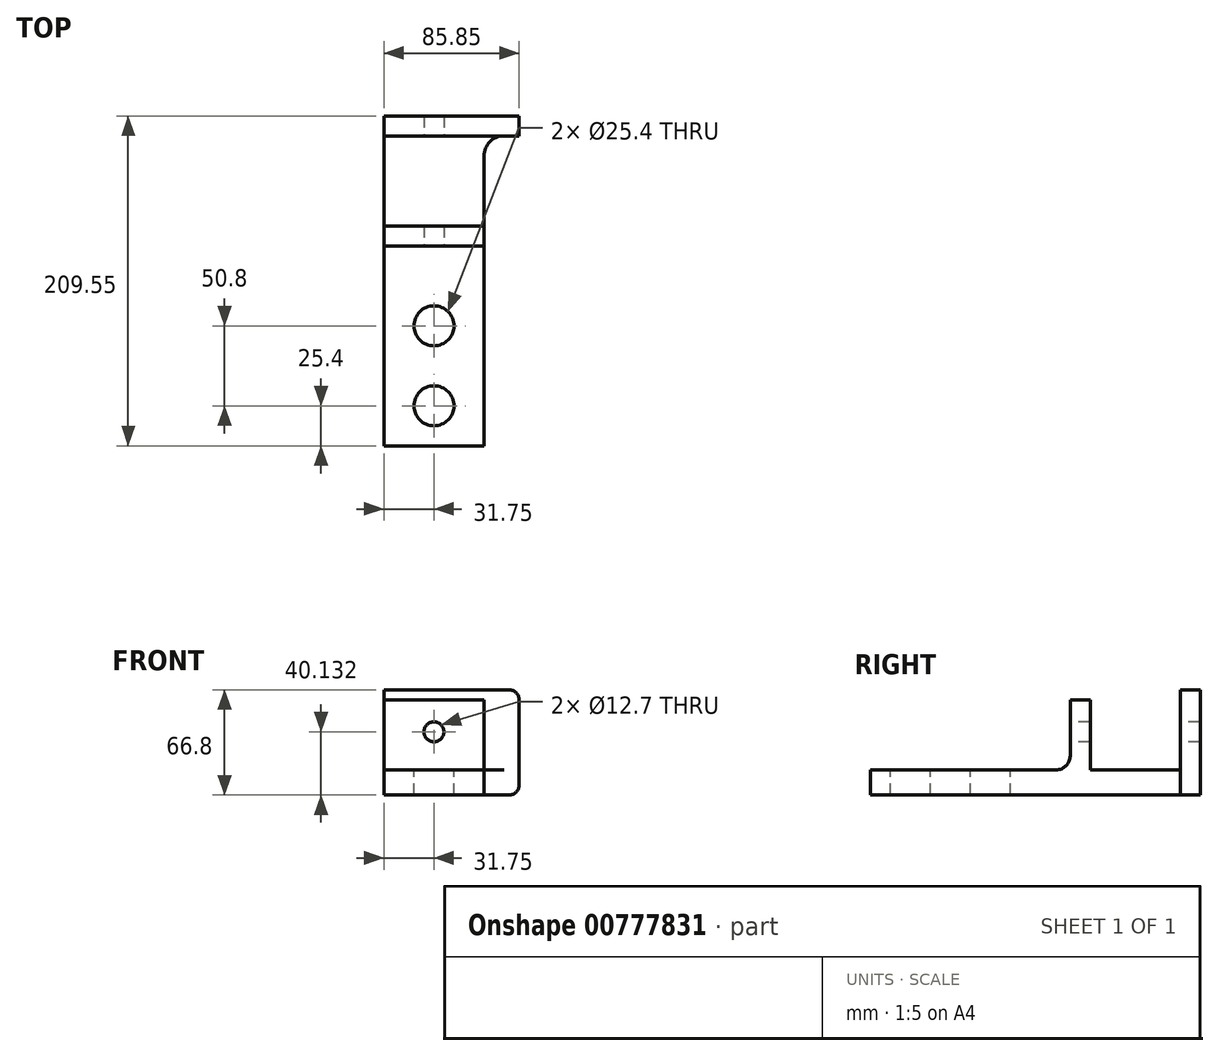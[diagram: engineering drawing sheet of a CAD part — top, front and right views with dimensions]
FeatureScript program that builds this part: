
annotation { "Feature Type Name" : "Feature", "Feature Type Description" : "" }
export const myFeature = defineFeature(function(context is Context, id is Id, definition is map)
    precondition{}
    {
        {
            var Q0;
            Q0=qCreatedBy(makeId("Right.planeOp"),FACE);
            var sketch = newSketch(context, id + "F0", { "sketchPlane" : qUnion([Q0])});
            skLineSegment(sketch, "E0", {"start": v(0, 0) * mm, "end": v(0, 66.8) * mm});
            skLineSegment(sketch, "E1", {"start": v(0, 66.8) * mm, "end": v(-12.7, 66.8) * mm});
            skLineSegment(sketch, "E2", {"start": v(-12.7, 66.8) * mm, "end": v(-12.7, 16) * mm});
            skLineSegment(sketch, "E3", {"start": v(-12.7, 16) * mm, "end": v(-69.85, 16) * mm});
            skLineSegment(sketch, "E4", {"start": v(-69.85, 16) * mm, "end": v(-69.85, 60.45) * mm});
            skLineSegment(sketch, "E5", {"start": v(-69.85, 60.45) * mm, "end": v(-82.55, 60.45) * mm});
            skLineSegment(sketch, "E6", {"start": v(-82.55, 60.45) * mm, "end": v(-82.55, 24.9) * mm});
            skLineSegment(sketch, "E7", {"start": v(-91.44, 16) * mm, "end": v(-209.55, 16) * mm});
            skLineSegment(sketch, "E8", {"start": v(-209.55, 16) * mm, "end": v(-209.55, 0) * mm});
            skLineSegment(sketch, "E9", {"start": v(-209.55, 0) * mm, "end": v(0, 0) * mm});
            skPoint(sketch, "E10.visualSharp", {"position": v(-82.55, 16) * mm});
            skArc(sketch, "E10.filletArc", {"start": v(-91.44, 16) * mm, "mid": v(-85.15, 18.6) * mm, "end": v(-82.55, 24.9) * mm});
            skSolve(sketch);
        }
        {
            var Q0;
            Q0 = qSketchRegion(id + "F0", true);
            extrude(context, id + "F1", {"entities" : qUnion([Q0]), "depth" : 54.1 * mm, "offsetDistance" : 25.4 * mm, "hasSecondDirection" : true, "secondDirectionOppositeDirection" : true, "secondDirectionDepth" : 31.75 * mm});
        }
        {
            var Q0;
            Q0=qCreatedBy(makeId("Top.planeOp"),FACE);
            var sketch = newSketch(context, id + "F2", { "sketchPlane" : qUnion([Q0])});
            skLineSegment(sketch, "E11.bottom", {"start": v(54.1, -209.55) * mm, "end": v(31.75, -209.55) * mm});
            skLineSegment(sketch, "E11.top", {"start": v(54.1, -12.7) * mm, "end": v(44.45, -12.7) * mm});
            skLineSegment(sketch, "E11.left", {"start": v(54.1, -209.55) * mm, "end": v(54.1, -12.7) * mm});
            skLineSegment(sketch, "E11.right", {"start": v(31.75, -209.55) * mm, "end": v(31.75, -25.4) * mm});
            skPoint(sketch, "E12.visualSharp", {"position": v(31.75, -12.7) * mm});
            skArc(sketch, "E12.filletArc", {"start": v(44.45, -12.7) * mm, "mid": v(35.47, -16.42) * mm, "end": v(31.75, -25.4) * mm});
            skSolve(sketch);
        }
        {
            var Q0;
            Q0 = qSketchRegion(id + "F2", true);
            extrude(context, id + "F3", {"entities" : qUnion([Q0]), "operationType" : NewBodyOperationType.REMOVE, "depth" : 66.8 * mm, "offsetDistance" : 25.4 * mm});
        }
        {
            var Q0;
            Q0=makeQuery(id+"F1.opExtrude","CAP_EDGE",EDGE,{"disambiguationData":[OSD([sQuery(id+"F0.wireOp",EDGE,"E9")])],"isStart":false});
            var Q1;
            Q1=makeQuery(id+"F1.opExtrude","CAP_EDGE",EDGE,{"disambiguationData":[OSD([sQuery(id+"F0.wireOp",EDGE,"E1")])],"isStart":false});
            fillet(context, id + "F4", {"entities" : qUnion([Q0, Q1]), "radius" : 6.35 * mm, "tangentPropagation" : true, "allowEdgeOverflow" : false});
        }
        {
            var Q0;
            Q0=makeQuery(id+"F1.opExtrude","SWEPT_FACE",FACE,{"disambiguationData":[OSD([sQuery(id+"F0.wireOp",EDGE,"E7")])]});
            var sketch = newSketch(context, id + "F5", { "sketchPlane" : qUnion([Q0])});
            skPoint(sketch, "E13", {"position": v(0, -133.35) * mm});
            skPoint(sketch, "E14", {"position": v(0, -184.15) * mm});
            skSolve(sketch);
        }
        {
            var Q0;
            Q0=sQuery(id+"F5.wireOp",VERTEX,"E13");
            var Q1;
            Q1=sQuery(id+"F5.wireOp",VERTEX,"E14");
            var Q2;
            Q2=makeQuery(id+"F1.opExtrude","SWEPT_BODY",BODY,{"disambiguationData":[OSD([sQuery(id+"F0.wireOp",EDGE,"E0"),sQuery(id+"F0.wireOp",EDGE,"E1"),sQuery(id+"F0.wireOp",EDGE,"E2"),sQuery(id+"F0.wireOp",EDGE,"E3"),sQuery(id+"F0.wireOp",EDGE,"E4"),sQuery(id+"F0.wireOp",EDGE,"E5"),sQuery(id+"F0.wireOp",EDGE,"E6"),sQuery(id+"F0.wireOp",EDGE,"E7"),sQuery(id+"F0.wireOp",EDGE,"E8"),sQuery(id+"F0.wireOp",EDGE,"E9"),sQuery(id+"F0.wireOp",EDGE,"E10.filletArc")])]});
            hole(context, id + "F6", {"style" : HoleStyle.SIMPLE, "endStyle" : HoleEndStyle.THROUGH, "holeDiameter" : 25.4 * mm, "majorDiameter" : 6.35 * mm, "isTappedThrough" : true, "tappedDepth" : 12.7 * mm, "tapClearance" : 3, "locations" : qUnion([Q0, Q1]), "scope" : qUnion([Q2])});
        }
        {
            var Q0;
            Q0=makeQuery(id+"F1.opExtrude","SWEPT_FACE",FACE,{"disambiguationData":[OSD([sQuery(id+"F0.wireOp",EDGE,"E6")])]});
            var sketch = newSketch(context, id + "F7", { "sketchPlane" : qUnion([Q0])});
            skPoint(sketch, "E15", {"position": v(0, 40.13) * mm});
            skSolve(sketch);
        }
        {
            var Q0;
            Q0=sQuery(id+"F7.wireOp",VERTEX,"E15");
            var Q1;
            Q1=makeQuery(id+"F1.opExtrude","SWEPT_BODY",BODY,{"disambiguationData":[OSD([sQuery(id+"F0.wireOp",EDGE,"E0"),sQuery(id+"F0.wireOp",EDGE,"E1"),sQuery(id+"F0.wireOp",EDGE,"E2"),sQuery(id+"F0.wireOp",EDGE,"E3"),sQuery(id+"F0.wireOp",EDGE,"E4"),sQuery(id+"F0.wireOp",EDGE,"E5"),sQuery(id+"F0.wireOp",EDGE,"E6"),sQuery(id+"F0.wireOp",EDGE,"E7"),sQuery(id+"F0.wireOp",EDGE,"E8"),sQuery(id+"F0.wireOp",EDGE,"E9"),sQuery(id+"F0.wireOp",EDGE,"E10.filletArc")])]});
            hole(context, id + "F8", {"style" : HoleStyle.SIMPLE, "endStyle" : HoleEndStyle.THROUGH, "holeDiameter" : 12.7 * mm, "majorDiameter" : 6.35 * mm, "isTappedThrough" : true, "tappedDepth" : 12.7 * mm, "tapClearance" : 3, "locations" : qUnion([Q0]), "scope" : qUnion([Q1])});
        }
    });
